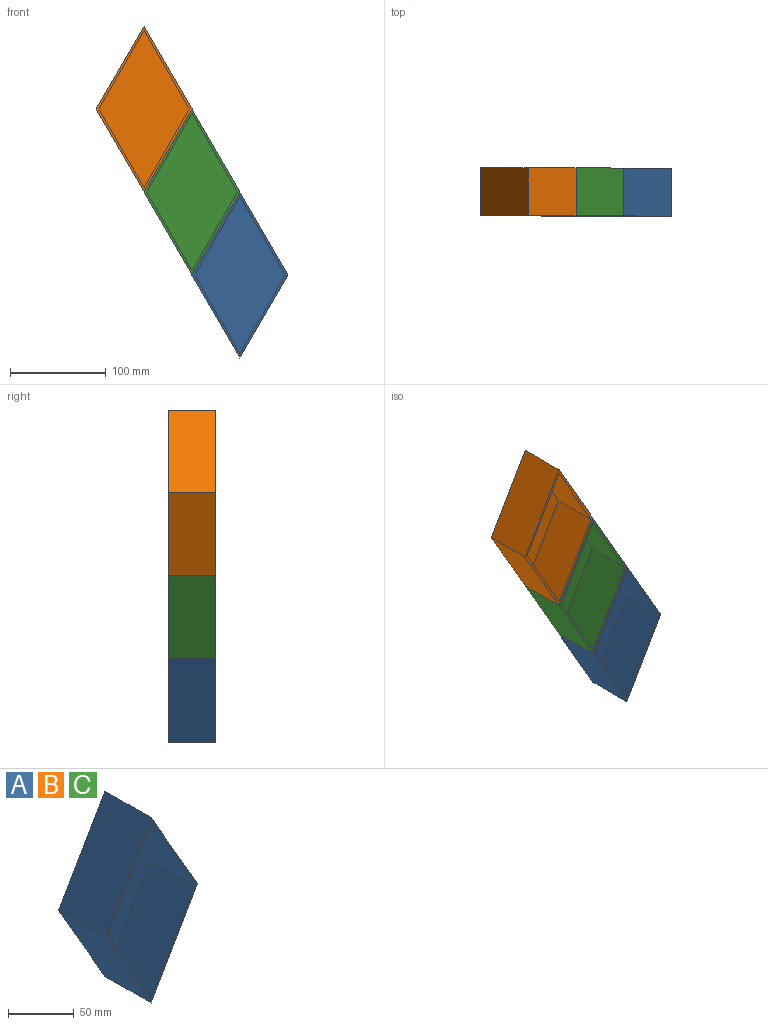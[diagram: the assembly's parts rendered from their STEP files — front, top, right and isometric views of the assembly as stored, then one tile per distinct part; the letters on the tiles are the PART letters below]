
ASSEMBLY  parts=3 mates=1
PART A: 11 faces, bbox 100x50x173.2 mm
  f0: plane 173.21x100mm, normal (0,-1,0), area 1008.1mm2, adj f1,f2,f3,f4,f6,f7,f8,f9
  f1: plane 86.6x50mm, normal (-0.87,0,0.5), area 5000mm2, adj f0,f2,f4,f5
  f2: plane 86.6x50mm, normal (-0.87,0,-0.5), area 5000mm2, adj f0,f1,f3,f5
  f3: plane 86.6x50mm, normal (0.87,0,-0.5), area 5000mm2, adj f0,f2,f4,f5
  f4: plane 86.6x50mm, normal (0.87,0,0.5), area 5000mm2, adj f0,f1,f3,f5
  f5: plane 173.21x100mm, normal (0,1,0), area 8660.3mm2, adj f1,f2,f3,f4
  f6: plane 81.41x48mm, normal (-0.87,0,-0.5), area 4512mm2, adj f0,f7,f9,f10
  f7: plane 81.41x48mm, normal (0.87,0,-0.5), area 4512mm2, adj f0,f6,f8,f10
  f8: plane 81.41x48mm, normal (0.87,0,0.5), area 4512mm2, adj f0,f7,f9,f10
  f9: plane 81.41x48mm, normal (-0.87,0,0.5), area 4512mm2, adj f0,f6,f8,f10
  f10: plane 162.81x94mm, normal (0,-1,0), area 7652.2mm2, adj f6,f7,f8,f9
PART B: same geometry as A
PART C: same geometry as A
PLACE A t=(56.32,-43.86,-163.66)mm
PLACE B t=(-43.68,-43.86,9.54)mm
PLACE C t=(6.32,-43.86,-77.06)mm
MATE fastened C.f1 <-> B.f3  axis (-0.87,0,0.5) through (-18.68,-18.86,-33.76)mm
